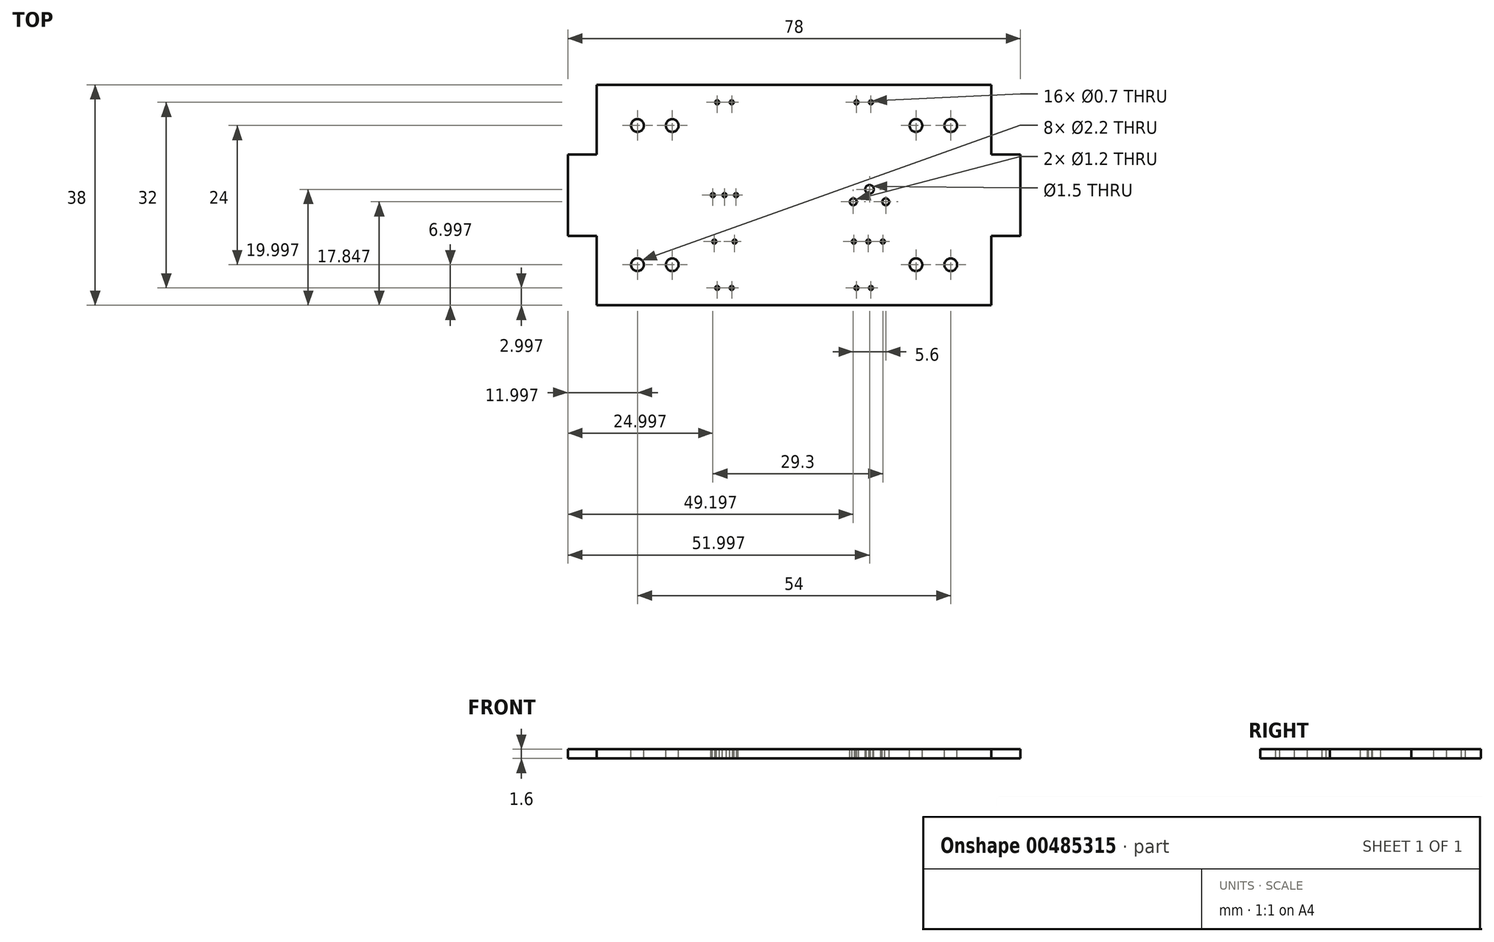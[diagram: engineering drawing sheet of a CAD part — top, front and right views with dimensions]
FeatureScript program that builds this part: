
annotation { "Feature Type Name" : "Feature", "Feature Type Description" : "" }
export const myFeature = defineFeature(function(context is Context, id is Id, definition is map)
    precondition{}
    {
        {
            var Q0;
            Q0=qCreatedBy(makeId("Top.planeOp"),FACE);
            var sketch = newSketch(context, id + "F0", { "sketchPlane" : qUnion([Q0])});
            skLineSegment(sketch, "E0", {"start": v(41.32, 33.2) * mm, "end": v(41.32, -3.8) * mm, "construction": true});
            skLineSegment(sketch, "E1.bottom", {"start": v(7.32, -4.3) * mm, "end": v(75.32, -4.3) * mm});
            skLineSegment(sketch, "E1.top", {"start": v(7.32, 33.7) * mm, "end": v(75.32, 33.7) * mm});
            skLineSegment(sketch, "E1.left", {"start": v(7.32, -4.3) * mm, "end": v(7.32, 33.7) * mm});
            skLineSegment(sketch, "E1.right", {"start": v(75.32, -4.3) * mm, "end": v(75.32, 33.7) * mm});
            skPoint(sketch, "E1.middle", {"position": v(41.32, 14.7) * mm});
            skLineSegment(sketch, "E2.bottom", {"start": v(80.32, 21.7) * mm, "end": v(2.32, 21.7) * mm});
            skLineSegment(sketch, "E2.top", {"start": v(80.32, 7.7) * mm, "end": v(2.32, 7.7) * mm});
            skLineSegment(sketch, "E2.left", {"start": v(80.32, 21.7) * mm, "end": v(80.32, 7.7) * mm});
            skLineSegment(sketch, "E2.right", {"start": v(2.32, 21.7) * mm, "end": v(2.32, 7.7) * mm});
            skSolve(sketch);
        }
        {
            var Q0;
            Q0=qSketchRegion(id+"F0",true);
            extrude(context, id + "F1", {"entities" : qUnion([Q0]), "depth" : 1.6 * mm});
        }
        {
            var Q0;
            Q0=makeQuery(id+"F1.opExtrude","CAP_FACE",FACE,{"disambiguationData":[OSD([sQuery(id+"F0.wireOp",EDGE,"E1.bottom"),sQuery(id+"F0.wireOp",EDGE,"E1.top"),sQuery(id+"F0.wireOp",EDGE,"E1.left"),sQuery(id+"F0.wireOp",EDGE,"E1.right")])],"isStart":false});
            var sketch = newSketch(context, id + "F2", { "sketchPlane" : qUnion([Q0])});
            skCircle(sketch, "E3", {"center": v(27.32, 14.7) * mm, "radius": 0.35 * mm});
            skLineSegment(sketch, "E4", {"start": v(41.32, 22.32) * mm, "end": v(41.32, 29.29) * mm, "construction": true});
            skCircle(sketch, "E5.1.0.0", {"center": v(29.32, 14.7) * mm, "radius": 0.35 * mm});
            skLineSegment(sketch, "E5.direction1", {"start": v(27.32, 14.7) * mm, "end": v(29.32, 14.7) * mm, "construction": true});
            skCircle(sketch, "E6.0.2.0", {"center": v(31.32, 14.7) * mm, "radius": 0.35 * mm});
            skLineSegment(sketch, "E7", {"start": v(28.32, 14.7) * mm, "end": v(2.32, 14.7) * mm, "construction": true});
            skSolve(sketch);
        }
        {
            var Q0;
            Q0=makeQuery(id+"F1.opExtrude","CAP_FACE",FACE,{"disambiguationData":[OSD([sQuery(id+"F0.wireOp",EDGE,"E1.bottom"),sQuery(id+"F0.wireOp",EDGE,"E1.top"),sQuery(id+"F0.wireOp",EDGE,"E1.left"),sQuery(id+"F0.wireOp",EDGE,"E1.right")])],"isStart":false});
            var sketch = newSketch(context, id + "F3", { "sketchPlane" : qUnion([Q0])});
            skLineSegment(sketch, "E8", {"start": v(54.32, 14.1) * mm, "end": v(54.32, 27.42) * mm, "construction": true});
            skLineSegment(sketch, "E9", {"start": v(41.32, 6.29) * mm, "end": v(41.32, 24.04) * mm, "construction": true});
            skLineSegment(sketch, "E10", {"start": v(51.17, 13.55) * mm, "end": v(51.87, 13.55) * mm, "construction": true});
            skLineSegment(sketch, "E11", {"start": v(51.52, 13.55) * mm, "end": v(51.52, 23.97) * mm, "construction": true});
            skLineSegment(sketch, "E12", {"start": v(53.82, 15.7) * mm, "end": v(54.82, 15.7) * mm, "construction": true});
            skLineSegment(sketch, "E13", {"start": v(54.32, 19.92) * mm, "end": v(54.32, 15.7) * mm, "construction": true});
            skArc(sketch, "E14.0.startCap", {"start": v(53.82, 15.45) * mm, "mid": v(53.57, 15.7) * mm, "end": v(53.82, 15.95) * mm});
            skArc(sketch, "E14.0.endCap", {"start": v(54.82, 15.95) * mm, "mid": v(55.07, 15.7) * mm, "end": v(54.82, 15.45) * mm});
            skLineSegment(sketch, "E14.0.left", {"start": v(53.82, 15.95) * mm, "end": v(54.82, 15.95) * mm});
            skLineSegment(sketch, "E14.0.right", {"start": v(53.82, 15.45) * mm, "end": v(54.82, 15.45) * mm});
            skLineSegment(sketch, "E15", {"start": v(50.5, 14.7) * mm, "end": v(53.65, 14.7) * mm, "construction": true});
            skArc(sketch, "E16.0.startCap", {"start": v(51.87, 13.8) * mm, "mid": v(52.12, 13.55) * mm, "end": v(51.87, 13.3) * mm});
            skArc(sketch, "E16.0.endCap", {"start": v(51.17, 13.3) * mm, "mid": v(50.92, 13.55) * mm, "end": v(51.17, 13.8) * mm});
            skLineSegment(sketch, "E16.0.left", {"start": v(51.17, 13.3) * mm, "end": v(51.87, 13.3) * mm});
            skLineSegment(sketch, "E16.0.right", {"start": v(51.17, 13.8) * mm, "end": v(51.87, 13.8) * mm});
            skArc(sketch, "E17.MirrorCS", {"start": v(57.47, 13.3) * mm, "mid": v(57.72, 13.55) * mm, "end": v(57.47, 13.8) * mm});
            skLineSegment(sketch, "E18.MirrorCS", {"start": v(57.47, 13.3) * mm, "end": v(56.77, 13.3) * mm});
            skLineSegment(sketch, "E19.MirrorCS", {"start": v(57.47, 13.8) * mm, "end": v(56.77, 13.8) * mm});
            skArc(sketch, "E20.MirrorCS", {"start": v(56.77, 13.8) * mm, "mid": v(56.52, 13.55) * mm, "end": v(56.77, 13.3) * mm});
            skLineSegment(sketch, "E21", {"start": v(50.5, 14.7) * mm, "end": v(2.32, 14.7) * mm, "construction": true});
            skCircle(sketch, "E22", {"center": v(51.52, 13.55) * mm, "radius": 0.6 * mm});
            skCircle(sketch, "E23", {"center": v(54.32, 15.7) * mm, "radius": 0.75 * mm});
            skCircle(sketch, "E24", {"center": v(57.12, 13.55) * mm, "radius": 0.6 * mm});
            skPoint(sketch, "E24.centerSnap0", {"position": v(57.12, 13.3) * mm});
            skSolve(sketch);
        }
        {
            var Q0;
            Q0=makeQuery(id+"F1.opExtrude","CAP_FACE",FACE,{"disambiguationData":[OSD([sQuery(id+"F0.wireOp",EDGE,"E1.bottom"),sQuery(id+"F0.wireOp",EDGE,"E1.top"),sQuery(id+"F0.wireOp",EDGE,"E1.left"),sQuery(id+"F0.wireOp",EDGE,"E1.right")])],"isStart":false});
            var sketch = newSketch(context, id + "F4", { "sketchPlane" : qUnion([Q0])});
            skCircle(sketch, "E25", {"center": v(51.62, 6.7) * mm, "radius": 0.35 * mm});
            skCircle(sketch, "E26.1.0.0", {"center": v(56.62, 6.7) * mm, "radius": 0.35 * mm});
            skLineSegment(sketch, "E26.direction1", {"start": v(51.62, 6.7) * mm, "end": v(56.62, 6.7) * mm, "construction": true});
            skLineSegment(sketch, "E27", {"start": v(41.32, 6.29) * mm, "end": v(41.32, 17.65) * mm, "construction": true});
            skLineSegment(sketch, "E28", {"start": v(54.12, 6.7) * mm, "end": v(54.12, 23.7) * mm, "construction": true});
            skCircle(sketch, "E29", {"center": v(54.12, 6.7) * mm, "radius": 0.35 * mm});
            skLineSegment(sketch, "E30", {"start": v(2.32, 14.7) * mm, "end": v(80.32, 14.7) * mm, "construction": true});
            skSolve(sketch);
        }
        {
            var Q0;
            Q0=makeQuery(id+"F1.opExtrude","CAP_FACE",FACE,{"disambiguationData":[OSD([sQuery(id+"F0.wireOp",EDGE,"E1.bottom"),sQuery(id+"F0.wireOp",EDGE,"E1.top"),sQuery(id+"F0.wireOp",EDGE,"E1.left"),sQuery(id+"F0.wireOp",EDGE,"E1.right")])],"isStart":false});
            var sketch = newSketch(context, id + "F5", { "sketchPlane" : qUnion([Q0])});
            skCircle(sketch, "E31", {"center": v(28.07, -1.3) * mm, "radius": 0.35 * mm});
            skCircle(sketch, "E32.1.0.0", {"center": v(30.57, -1.3) * mm, "radius": 0.35 * mm});
            skLineSegment(sketch, "E32.direction1", {"start": v(28.07, -1.3) * mm, "end": v(30.57, -1.3) * mm, "construction": true});
            skLineSegment(sketch, "E33", {"start": v(29.32, -1.3) * mm, "end": v(29.32, 26.14) * mm, "construction": true});
            skLineSegment(sketch, "E34", {"start": v(41.32, 33.7) * mm, "end": v(41.32, -4.3) * mm, "construction": true});
            skCircle(sketch, "E35.MirrorC", {"center": v(52.07, -1.3) * mm, "radius": 0.35 * mm});
            skCircle(sketch, "E36.MirrorC", {"center": v(54.57, -1.3) * mm, "radius": 0.35 * mm});
            skLineSegment(sketch, "E37", {"start": v(2.32, 14.7) * mm, "end": v(80.32, 14.7) * mm, "construction": true});
            skCircle(sketch, "E38.MirrorC", {"center": v(54.57, 30.7) * mm, "radius": 0.35 * mm});
            skCircle(sketch, "E39.MirrorC", {"center": v(52.07, 30.7) * mm, "radius": 0.35 * mm});
            skCircle(sketch, "E40.MirrorC", {"center": v(30.57, 30.7) * mm, "radius": 0.35 * mm});
            skCircle(sketch, "E41.MirrorC", {"center": v(28.07, 30.7) * mm, "radius": 0.35 * mm});
            skSolve(sketch);
        }
        {
            var Q0;
            Q0=makeQuery(id+"F1.opExtrude","CAP_FACE",FACE,{"disambiguationData":[OSD([sQuery(id+"F0.wireOp",EDGE,"E1.bottom"),sQuery(id+"F0.wireOp",EDGE,"E1.top"),sQuery(id+"F0.wireOp",EDGE,"E1.left"),sQuery(id+"F0.wireOp",EDGE,"E1.right")])],"isStart":false});
            var sketch = newSketch(context, id + "F6", { "sketchPlane" : qUnion([Q0])});
            skCircle(sketch, "E42", {"center": v(27.57, 6.7) * mm, "radius": 0.35 * mm});
            skCircle(sketch, "E43.1.0.0", {"center": v(31.07, 6.7) * mm, "radius": 0.35 * mm});
            skLineSegment(sketch, "E43.direction1", {"start": v(27.57, 6.7) * mm, "end": v(31.07, 6.7) * mm, "construction": true});
            skLineSegment(sketch, "E44", {"start": v(29.32, 13.4) * mm, "end": v(29.32, 6.7) * mm, "construction": true});
            skLineSegment(sketch, "E45", {"start": v(2.32, 14.7) * mm, "end": v(80.32, 14.7) * mm, "construction": true});
            skSolve(sketch);
        }
        {
            var Q0;
            Q0=qSketchRegion(id+"F4",true);
            var Q1;
            Q1=qSketchRegion(id+"F5",true);
            var Q2;
            Q2=qSketchRegion(id+"F6",true);
            var Q3;
            Q3=qSketchRegion(id+"F3",true);
            var Q4;
            Q4=qSketchRegion(id+"F2",true);
            extrude(context, id + "F7", {"entities" : qUnion([Q0, Q1, Q2, Q3, Q4]), "operationType" : NewBodyOperationType.REMOVE, "oppositeDirection" : true, "depth" : 4 * mm});
        }
        {
            var Q0;
            Q0=makeQuery(id+"F1.opExtrude","CAP_FACE",FACE,{"disambiguationData":[OSD([sQuery(id+"F0.wireOp",EDGE,"E1.bottom"),sQuery(id+"F0.wireOp",EDGE,"E1.top"),sQuery(id+"F0.wireOp",EDGE,"E1.left"),sQuery(id+"F0.wireOp",EDGE,"E1.right")])],"isStart":false});
            var sketch = newSketch(context, id + "F8", { "sketchPlane" : qUnion([Q0])});
            skLineSegment(sketch, "E46", {"start": v(41.32, 33.7) * mm, "end": v(41.32, -4.3) * mm, "construction": true});
            skCircle(sketch, "E47", {"center": v(62.32, 26.7) * mm, "radius": 1.1 * mm});
            skCircle(sketch, "E48.MirrorC", {"center": v(20.32, 26.7) * mm, "radius": 1.1 * mm});
            skLineSegment(sketch, "E49", {"start": v(41.32, 14.7) * mm, "end": v(80.32, 14.7) * mm, "construction": true});
            skCircle(sketch, "E50", {"center": v(68.32, 2.7) * mm, "radius": 1.1 * mm});
            skCircle(sketch, "E51.MirrorC", {"center": v(14.32, 2.7) * mm, "radius": 1.1 * mm});
            skCircle(sketch, "E52.MirrorC", {"center": v(62.32, 2.7) * mm, "radius": 1.1 * mm});
            skCircle(sketch, "E53.MirrorC", {"center": v(20.32, 2.7) * mm, "radius": 1.1 * mm});
            skCircle(sketch, "E54.MirrorC", {"center": v(68.32, 26.7) * mm, "radius": 1.1 * mm});
            skCircle(sketch, "E55.MirrorC", {"center": v(14.32, 26.7) * mm, "radius": 1.1 * mm});
            skSolve(sketch);
        }
        {
            var Q0;
            Q0=qSketchRegion(id+"F8",true);
            extrude(context, id + "F9", {"entities" : qUnion([Q0]), "operationType" : NewBodyOperationType.REMOVE, "oppositeDirection" : true, "depth" : 25 * mm});
        }
    });
